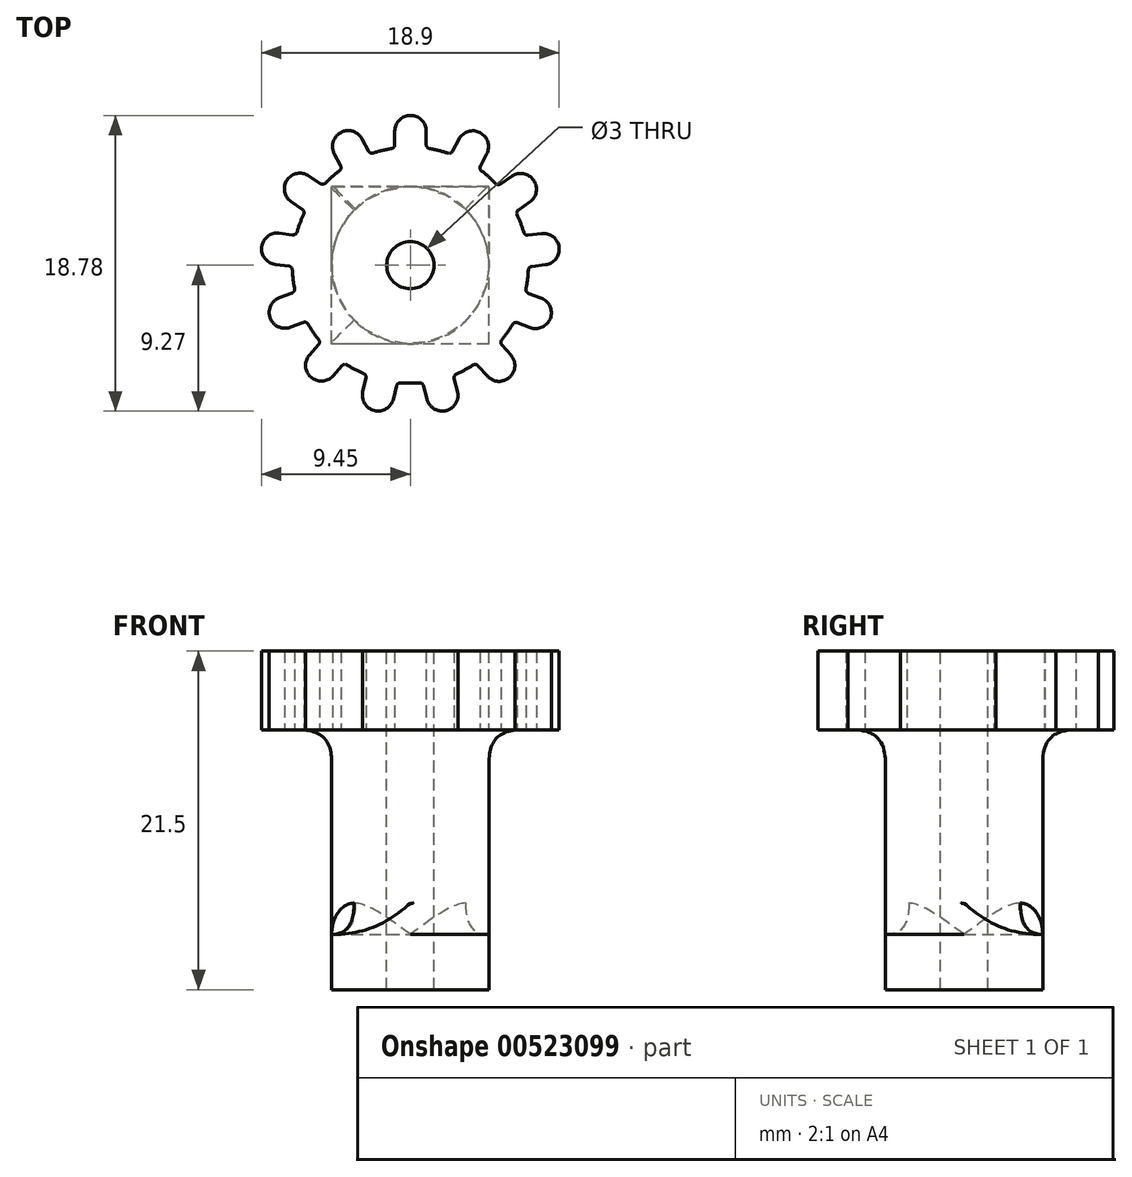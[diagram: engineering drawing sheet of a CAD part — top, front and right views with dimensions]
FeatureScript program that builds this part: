
annotation { "Feature Type Name" : "Feature", "Feature Type Description" : "" }
export const myFeature = defineFeature(function(context is Context, id is Id, definition is map)
    precondition{}
    {
        {
            var Q0;
            Q0=qCreatedBy(makeId("Top.planeOp"),FACE);
            var sketch = newSketch(context, id + "F0", { "sketchPlane" : qUnion([Q0])});
            skLineSegment(sketch, "E0.bottom", {"start": v(5, -5) * mm, "end": v(-5, -5) * mm});
            skLineSegment(sketch, "E0.top", {"start": v(5, 5) * mm, "end": v(-5, 5) * mm});
            skLineSegment(sketch, "E0.left", {"start": v(5, -5) * mm, "end": v(5, 5) * mm});
            skLineSegment(sketch, "E0.right", {"start": v(-5, -5) * mm, "end": v(-5, 5) * mm});
            skPoint(sketch, "E0.middle", {"position": v(0, 0) * mm});
            skSolve(sketch);
        }
        {
            var Q0;
            Q0=makeQuery(id+"F0.imprint","IMPRINT",FACE,{"disambiguationData":[TD([[makeQuery(id+"F0.imprint","IMPRINT",EDGE,{"derivedFrom":sQuery(id+"F0.wireOp",EDGE,"E0.bottom")}),-1.0]])]});
            extrude(context, id + "F1", {"entities" : qUnion([Q0]), "depth" : 3.5 * mm, "offsetDistance" : 25 * mm});
        }
        {
            var Q0;
            Q0=makeQuery(id+"F1.opExtrude","CAP_FACE",FACE,{"disambiguationData":[OSD([sQuery(id+"F0.wireOp",EDGE,"E0.bottom"),sQuery(id+"F0.wireOp",EDGE,"E0.top"),sQuery(id+"F0.wireOp",EDGE,"E0.left"),sQuery(id+"F0.wireOp",EDGE,"E0.right")])],"isStart":false});
            var sketch = newSketch(context, id + "F2", { "sketchPlane" : qUnion([Q0])});
            skCircle(sketch, "E1", {"center": v(0, 0) * mm, "radius": 5 * mm});
            skSolve(sketch);
        }
        {
            var Q0;
            Q0 = qSketchRegion(id + "F2", true);
            extrude(context, id + "F3", {"entities" : qUnion([Q0]), "operationType" : NewBodyOperationType.ADD, "depth" : 13 * mm, "offsetDistance" : 25 * mm});
        }
        {
            var Q0;
            Q0=makeQuery(id+"F3.opExtrude","CAP_FACE",FACE,{"disambiguationData":[OSD([sQuery(id+"F2.wireOp",EDGE,"E1")])],"isStart":false});
            var sketch = newSketch(context, id + "F4", { "sketchPlane" : qUnion([Q0])});
            skCircle(sketch, "E2", {"center": v(0, 0) * mm, "radius": 1.5 * mm});
            skSolve(sketch);
        }
        {
            var Q0;
            Q0=makeQuery(id+"F4.imprint","IMPRINT",FACE,{"disambiguationData":[TD([[makeQuery(id+"F4.imprint","IMPRINT",EDGE,{"derivedFrom":sQuery(id+"F4.wireOp",EDGE,"E2")}),1.0]])]});
            extrude(context, id + "F5", {"entities" : qUnion([Q0]), "operationType" : NewBodyOperationType.REMOVE, "endBound" : BoundingType.THROUGH_ALL, "oppositeDirection" : true, "depth" : 25 * mm, "offsetDistance" : 25 * mm});
        }
        {
            var Q0;
            Q0=makeQuery(id+"F3.opExtrude","CAP_FACE",FACE,{"disambiguationData":[OSD([sQuery(id+"F2.wireOp",EDGE,"E1")])],"isStart":false});
            var sketch = newSketch(context, id + "F6", { "sketchPlane" : qUnion([Q0])});
            skArc(sketch, "E3", {"start": v(-1.2, 7.4) * mm, "mid": v(-1.78, 7.28) * mm, "end": v(-2.36, 7.12) * mm});
            skLineSegment(sketch, "E4", {"start": v(0.01, 9.51) * mm, "end": v(0.01, 9.51) * mm});
            skLineSegment(sketch, "E5", {"start": v(1.01, 8.51) * mm, "end": v(1.01, 7.65) * mm});
            skLineSegment(sketch, "E6", {"start": v(-0.99, 8.51) * mm, "end": v(-0.99, 7.65) * mm});
            skPoint(sketch, "E7.visualSharp", {"position": v(-0.99, 7.43) * mm});
            skArc(sketch, "E7.filletArc", {"start": v(-1.2, 7.4) * mm, "mid": v(-1.05, 7.49) * mm, "end": v(-0.99, 7.65) * mm});
            skPoint(sketch, "E8.visualSharp", {"position": v(1.01, 7.43) * mm});
            skArc(sketch, "E8.filletArc", {"start": v(1.01, 7.65) * mm, "mid": v(1.07, 7.48) * mm, "end": v(1.22, 7.4) * mm});
            skPoint(sketch, "E9.visualSharp", {"position": v(-0.99, 9.51) * mm});
            skArc(sketch, "E9.filletArc", {"start": v(0.01, 9.51) * mm, "mid": v(-0.7, 9.22) * mm, "end": v(-0.99, 8.51) * mm});
            skPoint(sketch, "E10.visualSharp", {"position": v(1.01, 9.51) * mm});
            skArc(sketch, "E10.filletArc", {"start": v(1.01, 8.51) * mm, "mid": v(0.72, 9.22) * mm, "end": v(0.01, 9.51) * mm});
            skArc(sketch, "E11.1.0", {"start": v(-4.5, 6) * mm, "mid": v(-4.4, 6.14) * mm, "end": v(-4.43, 6.31) * mm});
            skLineSegment(sketch, "E11.1.1", {"start": v(-4.83, 7.08) * mm, "end": v(-4.43, 6.31) * mm});
            skArc(sketch, "E11.1.2", {"start": v(-4.41, 8.43) * mm, "mid": v(-4.9, 7.84) * mm, "end": v(-4.83, 7.08) * mm});
            skArc(sketch, "E11.1.3", {"start": v(-3.06, 8) * mm, "mid": v(-3.65, 8.5) * mm, "end": v(-4.41, 8.43) * mm});
            skLineSegment(sketch, "E11.1.4", {"start": v(-3.06, 8) * mm, "end": v(-2.66, 7.24) * mm});
            skArc(sketch, "E11.1.5", {"start": v(-2.66, 7.24) * mm, "mid": v(-2.53, 7.13) * mm, "end": v(-2.36, 7.12) * mm});
            skArc(sketch, "E11.2.0", {"start": v(-6.77, 3.22) * mm, "mid": v(-6.76, 3.4) * mm, "end": v(-6.86, 3.53) * mm});
            skLineSegment(sketch, "E11.2.1", {"start": v(-7.57, 4.02) * mm, "end": v(-6.86, 3.53) * mm});
            skArc(sketch, "E11.2.2", {"start": v(-7.82, 5.41) * mm, "mid": v(-7.98, 4.67) * mm, "end": v(-7.57, 4.02) * mm});
            skArc(sketch, "E11.2.3", {"start": v(-6.43, 5.67) * mm, "mid": v(-7.18, 5.83) * mm, "end": v(-7.82, 5.41) * mm});
            skLineSegment(sketch, "E11.2.4", {"start": v(-6.43, 5.67) * mm, "end": v(-5.72, 5.18) * mm});
            skArc(sketch, "E11.2.5", {"start": v(-5.72, 5.18) * mm, "mid": v(-5.55, 5.13) * mm, "end": v(-5.4, 5.2) * mm});
            skArc(sketch, "E11.3.0", {"start": v(-7.5, -0.3) * mm, "mid": v(-7.56, -0.14) * mm, "end": v(-7.71, -0.06) * mm});
            skLineSegment(sketch, "E11.3.1", {"start": v(-8.57, 0.05) * mm, "end": v(-7.71, -0.06) * mm});
            skArc(sketch, "E11.3.2", {"start": v(-9.44, 1.16) * mm, "mid": v(-9.24, 0.42) * mm, "end": v(-8.57, 0.05) * mm});
            skArc(sketch, "E11.3.3", {"start": v(-8.33, 2.03) * mm, "mid": v(-9.07, 1.83) * mm, "end": v(-9.44, 1.16) * mm});
            skLineSegment(sketch, "E11.3.4", {"start": v(-8.33, 2.03) * mm, "end": v(-7.47, 1.93) * mm});
            skArc(sketch, "E11.3.5", {"start": v(-7.47, 1.93) * mm, "mid": v(-7.3, 1.97) * mm, "end": v(-7.2, 2.1) * mm});
            skArc(sketch, "E11.4.0", {"start": v(-6.5, -3.75) * mm, "mid": v(-6.63, -3.64) * mm, "end": v(-6.8, -3.64) * mm});
            skLineSegment(sketch, "E11.4.1", {"start": v(-7.61, -3.94) * mm, "end": v(-6.8, -3.64) * mm});
            skArc(sketch, "E11.4.2", {"start": v(-8.9, -3.36) * mm, "mid": v(-8.38, -3.92) * mm, "end": v(-7.61, -3.94) * mm});
            skArc(sketch, "E11.4.3", {"start": v(-8.32, -2.07) * mm, "mid": v(-8.88, -2.6) * mm, "end": v(-8.9, -3.36) * mm});
            skLineSegment(sketch, "E11.4.4", {"start": v(-8.32, -2.07) * mm, "end": v(-7.5, -1.77) * mm});
            skArc(sketch, "E11.4.5", {"start": v(-7.5, -1.77) * mm, "mid": v(-7.38, -1.65) * mm, "end": v(-7.35, -1.48) * mm});
            skArc(sketch, "E11.5.0", {"start": v(-4.01, -6.34) * mm, "mid": v(-4.18, -6.3) * mm, "end": v(-4.33, -6.38) * mm});
            skLineSegment(sketch, "E11.5.1", {"start": v(-4.9, -7.03) * mm, "end": v(-4.33, -6.38) * mm});
            skArc(sketch, "E11.5.2", {"start": v(-6.32, -7.11) * mm, "mid": v(-5.6, -7.36) * mm, "end": v(-4.9, -7.03) * mm});
            skArc(sketch, "E11.5.3", {"start": v(-6.4, -5.7) * mm, "mid": v(-6.65, -6.43) * mm, "end": v(-6.32, -7.11) * mm});
            skLineSegment(sketch, "E11.5.4", {"start": v(-6.4, -5.7) * mm, "end": v(-5.83, -5.05) * mm});
            skArc(sketch, "E11.5.5", {"start": v(-5.83, -5.05) * mm, "mid": v(-5.77, -4.9) * mm, "end": v(-5.82, -4.73) * mm});
            skArc(sketch, "E11.6.0", {"start": v(-0.6, -7.48) * mm, "mid": v(-0.77, -7.52) * mm, "end": v(-0.87, -7.66) * mm});
            skLineSegment(sketch, "E11.6.1", {"start": v(-1.08, -8.5) * mm, "end": v(-0.87, -7.66) * mm});
            skArc(sketch, "E11.6.2", {"start": v(-2.29, -9.23) * mm, "mid": v(-1.53, -9.12) * mm, "end": v(-1.08, -8.5) * mm});
            skArc(sketch, "E11.6.3", {"start": v(-3.02, -8.02) * mm, "mid": v(-2.9, -8.78) * mm, "end": v(-2.29, -9.23) * mm});
            skLineSegment(sketch, "E11.6.4", {"start": v(-3.02, -8.02) * mm, "end": v(-2.81, -7.18) * mm});
            skArc(sketch, "E11.6.5", {"start": v(-2.81, -7.18) * mm, "mid": v(-2.83, -7.01) * mm, "end": v(-2.96, -6.9) * mm});
            skArc(sketch, "E11.7.0", {"start": v(2.94, -6.9) * mm, "mid": v(2.8, -7.02) * mm, "end": v(2.8, -7.2) * mm});
            skLineSegment(sketch, "E11.7.1", {"start": v(3, -8.03) * mm, "end": v(2.8, -7.2) * mm});
            skArc(sketch, "E11.7.2", {"start": v(2.27, -9.24) * mm, "mid": v(2.88, -8.79) * mm, "end": v(3, -8.03) * mm});
            skArc(sketch, "E11.7.3", {"start": v(1.06, -8.5) * mm, "mid": v(1.5, -9.12) * mm, "end": v(2.27, -9.24) * mm});
            skLineSegment(sketch, "E11.7.4", {"start": v(1.06, -8.5) * mm, "end": v(0.85, -7.67) * mm});
            skArc(sketch, "E11.7.5", {"start": v(0.85, -7.67) * mm, "mid": v(0.75, -7.52) * mm, "end": v(0.59, -7.48) * mm});
            skArc(sketch, "E11.8.0", {"start": v(5.8, -4.75) * mm, "mid": v(5.75, -4.91) * mm, "end": v(5.81, -5.07) * mm});
            skLineSegment(sketch, "E11.8.1", {"start": v(6.39, -5.72) * mm, "end": v(5.81, -5.07) * mm});
            skArc(sketch, "E11.8.2", {"start": v(6.3, -7.13) * mm, "mid": v(6.64, -6.44) * mm, "end": v(6.39, -5.72) * mm});
            skArc(sketch, "E11.8.3", {"start": v(4.89, -7.04) * mm, "mid": v(5.58, -7.38) * mm, "end": v(6.3, -7.13) * mm});
            skLineSegment(sketch, "E11.8.4", {"start": v(4.89, -7.04) * mm, "end": v(4.31, -6.4) * mm});
            skArc(sketch, "E11.8.5", {"start": v(4.31, -6.4) * mm, "mid": v(4.16, -6.31) * mm, "end": v(4, -6.35) * mm});
            skArc(sketch, "E11.9.0", {"start": v(7.35, -1.5) * mm, "mid": v(7.37, -1.68) * mm, "end": v(7.5, -1.79) * mm});
            skLineSegment(sketch, "E11.9.1", {"start": v(8.31, -2.1) * mm, "end": v(7.5, -1.79) * mm});
            skArc(sketch, "E11.9.2", {"start": v(8.9, -3.38) * mm, "mid": v(8.87, -2.62) * mm, "end": v(8.31, -2.1) * mm});
            skArc(sketch, "E11.9.3", {"start": v(7.6, -3.97) * mm, "mid": v(8.37, -3.94) * mm, "end": v(8.9, -3.38) * mm});
            skLineSegment(sketch, "E11.9.4", {"start": v(7.6, -3.97) * mm, "end": v(6.8, -3.66) * mm});
            skArc(sketch, "E11.9.5", {"start": v(6.8, -3.66) * mm, "mid": v(6.62, -3.66) * mm, "end": v(6.49, -3.77) * mm});
            skArc(sketch, "E12.2.10.0", {"start": v(7.2, 2.08) * mm, "mid": v(7.3, 1.94) * mm, "end": v(7.48, 1.9) * mm});
            skLineSegment(sketch, "E12.4.10.0", {"start": v(8.33, 2) * mm, "end": v(7.48, 1.9) * mm});
            skArc(sketch, "E12.7.10.0", {"start": v(9.45, 1.14) * mm, "mid": v(9.07, 1.8) * mm, "end": v(8.33, 2) * mm});
            skArc(sketch, "E12.11.10.0", {"start": v(8.57, 0.02) * mm, "mid": v(9.24, 0.4) * mm, "end": v(9.45, 1.14) * mm});
            skLineSegment(sketch, "E12.15.10.0", {"start": v(8.57, 0.02) * mm, "end": v(7.71, -0.08) * mm});
            skArc(sketch, "E12.18.10.0", {"start": v(7.71, -0.08) * mm, "mid": v(7.56, -0.16) * mm, "end": v(7.5, -0.32) * mm});
            skArc(sketch, "E12.2.11.0", {"start": v(5.41, 5.2) * mm, "mid": v(5.57, 5.12) * mm, "end": v(5.73, 5.16) * mm});
            skLineSegment(sketch, "E12.4.11.0", {"start": v(6.45, 5.65) * mm, "end": v(5.73, 5.16) * mm});
            skArc(sketch, "E12.7.11.0", {"start": v(7.84, 5.4) * mm, "mid": v(7.2, 5.81) * mm, "end": v(6.45, 5.65) * mm});
            skArc(sketch, "E12.11.11.0", {"start": v(7.58, 4) * mm, "mid": v(8, 4.65) * mm, "end": v(7.84, 5.4) * mm});
            skLineSegment(sketch, "E12.15.11.0", {"start": v(7.58, 4) * mm, "end": v(6.87, 3.51) * mm});
            skArc(sketch, "E12.18.11.0", {"start": v(6.87, 3.51) * mm, "mid": v(6.77, 3.37) * mm, "end": v(6.78, 3.2) * mm});
            skArc(sketch, "E13.2.12.0", {"start": v(2.38, 7.11) * mm, "mid": v(2.55, 7.12) * mm, "end": v(2.68, 7.23) * mm});
            skLineSegment(sketch, "E13.4.12.0", {"start": v(3.08, 8) * mm, "end": v(2.68, 7.23) * mm});
            skArc(sketch, "E13.7.12.0", {"start": v(4.43, 8.42) * mm, "mid": v(3.67, 8.49) * mm, "end": v(3.08, 8) * mm});
            skArc(sketch, "E13.11.12.0", {"start": v(4.85, 7.07) * mm, "mid": v(4.92, 7.83) * mm, "end": v(4.43, 8.42) * mm});
            skLineSegment(sketch, "E13.15.12.0", {"start": v(4.85, 7.07) * mm, "end": v(4.45, 6.3) * mm});
            skArc(sketch, "E13.18.12.0", {"start": v(4.45, 6.3) * mm, "mid": v(4.43, 6.13) * mm, "end": v(4.52, 5.98) * mm});
            skArc(sketch, "E14.trimOffspring", {"start": v(-4.5, 6) * mm, "mid": v(-4.96, 5.62) * mm, "end": v(-5.4, 5.2) * mm});
            skArc(sketch, "E15.trimOffspring", {"start": v(-6.77, 3.22) * mm, "mid": v(-7, 2.67) * mm, "end": v(-7.2, 2.1) * mm});
            skArc(sketch, "E16.trimOffspring", {"start": v(-7.5, -0.3) * mm, "mid": v(-7.45, -0.9) * mm, "end": v(-7.35, -1.48) * mm});
            skArc(sketch, "E17.trimOffspring", {"start": v(-6.5, -3.75) * mm, "mid": v(-6.18, -4.25) * mm, "end": v(-5.82, -4.73) * mm});
            skArc(sketch, "E18.trimOffspring", {"start": v(-4.01, -6.34) * mm, "mid": v(-3.5, -6.64) * mm, "end": v(-2.96, -6.9) * mm});
            skArc(sketch, "E19.trimOffspring", {"start": v(-0.6, -7.48) * mm, "mid": v(-0.01, -7.5) * mm, "end": v(0.59, -7.48) * mm});
            skArc(sketch, "E20.trimOffspring", {"start": v(2.94, -6.9) * mm, "mid": v(3.48, -6.65) * mm, "end": v(4, -6.35) * mm});
            skArc(sketch, "E21.trimOffspring", {"start": v(5.8, -4.75) * mm, "mid": v(6.17, -4.27) * mm, "end": v(6.49, -3.77) * mm});
            skArc(sketch, "E22.trimOffspring", {"start": v(7.35, -1.5) * mm, "mid": v(7.44, -0.92) * mm, "end": v(7.5, -0.32) * mm});
            skArc(sketch, "E23.trimOffspring", {"start": v(7.2, 2.08) * mm, "mid": v(7.02, 2.65) * mm, "end": v(6.78, 3.2) * mm});
            skArc(sketch, "E24.trimOffspring", {"start": v(5.41, 5.2) * mm, "mid": v(4.98, 5.6) * mm, "end": v(4.52, 5.98) * mm});
            skArc(sketch, "E25.trimOffspring", {"start": v(2.38, 7.11) * mm, "mid": v(1.8, 7.28) * mm, "end": v(1.22, 7.4) * mm});
            skSolve(sketch);
        }
        {
            var Q0;
            Q0=makeQuery(id+"F6.imprint","IMPRINT",FACE,{"disambiguationData":[TD([[makeQuery(id+"F6.imprint","IMPRINT",EDGE,{"derivedFrom":sQuery(id+"F6.wireOp",EDGE,"E3")}),1.0]])]});
            extrude(context, id + "F7", {"entities" : qUnion([Q0]), "operationType" : NewBodyOperationType.ADD, "depth" : 5 * mm, "offsetDistance" : 25 * mm});
        }
        {
            var Q0;
            Q0=makeQuery(id+"F3.opExtrude","CAP_FACE",FACE,{"disambiguationData":[OSD([sQuery(id+"F2.wireOp",EDGE,"E1")])],"isStart":false});
            extrude(context, id + "F8", {"entities" : qUnion([Q0]), "operationType" : NewBodyOperationType.ADD, "depth" : 5 * mm, "offsetDistance" : 25 * mm});
        }
        {
            var Q0;
            Q0=makeQuery(id+"F3.opExtrude","CAP_EDGE",EDGE,{"disambiguationData":[OSD([sQuery(id+"F2.wireOp",EDGE,"E1")])],"isStart":false});
            fillet(context, id + "F9", {"entities" : qUnion([Q0]), "radius" : 2 * mm, "rho" : 0.5, "crossSection" : FilletCrossSection.CONIC, "allowEdgeOverflow" : false});
        }
        {
            var Q0;
            {var subQ0=sQuery(id+"F0.wireOp",EDGE,"E0.bottom");var subQ1=sQuery(id+"F0.wireOp",EDGE,"E0.left");var subQ2=sQuery(id+"F2.wireOp",EDGE,"E1");Q0=makeQuery(id+"F3.boolean.opBoolean","SPLIT",EDGE,{"disambiguationData":[TD([makeQuery(id+"F1.opExtrude","SWEPT_FACE",FACE,{"disambiguationData":[OSD([subQ0])]}),makeQuery(id+"F1.opExtrude","CAP_FACE",FACE,{"disambiguationData":[OSD([subQ0,sQuery(id+"F0.wireOp",EDGE,"E0.top"),subQ1,sQuery(id+"F0.wireOp",EDGE,"E0.right")])],"isStart":false}),makeQuery(id+"F1.opExtrude","SWEPT_FACE",FACE,{"disambiguationData":[OSD([subQ1])]}),makeQuery(id+"F3.opExtrude","SWEPT_FACE",FACE,{"disambiguationData":[OSD([subQ2])]})])],"derivedFrom":makeQuery(id+"F3.opExtrude","CAP_EDGE",EDGE,{"disambiguationData":[OSD([subQ2])],"isStart":true})});}
            var Q1;
            {var subQ0=sQuery(id+"F0.wireOp",EDGE,"E0.left");var subQ1=sQuery(id+"F0.wireOp",EDGE,"E0.top");var subQ2=sQuery(id+"F2.wireOp",EDGE,"E1");Q1=makeQuery(id+"F3.boolean.opBoolean","SPLIT",EDGE,{"disambiguationData":[TD([makeQuery(id+"F1.opExtrude","CAP_FACE",FACE,{"disambiguationData":[OSD([sQuery(id+"F0.wireOp",EDGE,"E0.bottom"),subQ1,subQ0,sQuery(id+"F0.wireOp",EDGE,"E0.right")])],"isStart":false}),makeQuery(id+"F1.opExtrude","SWEPT_FACE",FACE,{"disambiguationData":[OSD([subQ1])]}),makeQuery(id+"F1.opExtrude","SWEPT_FACE",FACE,{"disambiguationData":[OSD([subQ0])]}),makeQuery(id+"F3.opExtrude","SWEPT_FACE",FACE,{"disambiguationData":[OSD([subQ2])]})])],"derivedFrom":makeQuery(id+"F3.opExtrude","CAP_EDGE",EDGE,{"disambiguationData":[OSD([subQ2])],"isStart":true})});}
            var Q2;
            {var subQ0=sQuery(id+"F0.wireOp",EDGE,"E0.bottom");var subQ1=sQuery(id+"F0.wireOp",EDGE,"E0.right");var subQ2=sQuery(id+"F2.wireOp",EDGE,"E1");Q2=makeQuery(id+"F3.boolean.opBoolean","SPLIT",EDGE,{"disambiguationData":[TD([makeQuery(id+"F1.opExtrude","SWEPT_FACE",FACE,{"disambiguationData":[OSD([subQ0])]}),makeQuery(id+"F1.opExtrude","CAP_FACE",FACE,{"disambiguationData":[OSD([subQ0,sQuery(id+"F0.wireOp",EDGE,"E0.top"),sQuery(id+"F0.wireOp",EDGE,"E0.left"),subQ1])],"isStart":false}),makeQuery(id+"F1.opExtrude","SWEPT_FACE",FACE,{"disambiguationData":[OSD([subQ1])]}),makeQuery(id+"F3.opExtrude","SWEPT_FACE",FACE,{"disambiguationData":[OSD([subQ2])]})])],"derivedFrom":makeQuery(id+"F3.opExtrude","CAP_EDGE",EDGE,{"disambiguationData":[OSD([subQ2])],"isStart":true})});}
            var Q3;
            {var subQ0=sQuery(id+"F0.wireOp",EDGE,"E0.right");var subQ1=sQuery(id+"F0.wireOp",EDGE,"E0.top");var subQ2=sQuery(id+"F2.wireOp",EDGE,"E1");Q3=makeQuery(id+"F3.boolean.opBoolean","SPLIT",EDGE,{"disambiguationData":[TD([makeQuery(id+"F1.opExtrude","CAP_FACE",FACE,{"disambiguationData":[OSD([sQuery(id+"F0.wireOp",EDGE,"E0.bottom"),subQ1,sQuery(id+"F0.wireOp",EDGE,"E0.left"),subQ0])],"isStart":false}),makeQuery(id+"F1.opExtrude","SWEPT_FACE",FACE,{"disambiguationData":[OSD([subQ1])]}),makeQuery(id+"F1.opExtrude","SWEPT_FACE",FACE,{"disambiguationData":[OSD([subQ0])]}),makeQuery(id+"F3.opExtrude","SWEPT_FACE",FACE,{"disambiguationData":[OSD([subQ2])]})])],"derivedFrom":makeQuery(id+"F3.opExtrude","CAP_EDGE",EDGE,{"disambiguationData":[OSD([subQ2])],"isStart":true})});}
            fillet(context, id + "F10", {"entities" : qUnion([Q0, Q1, Q2, Q3]), "radius" : 2 * mm, "rho" : 0.5, "crossSection" : FilletCrossSection.CONIC, "allowEdgeOverflow" : false});
        }
    });
